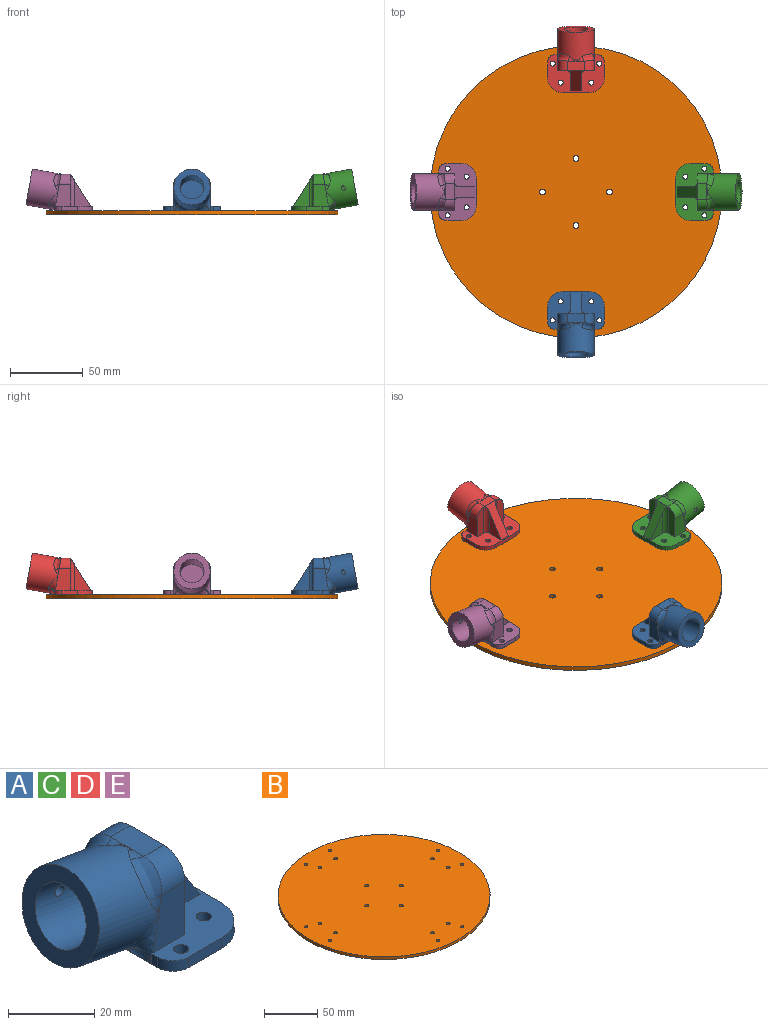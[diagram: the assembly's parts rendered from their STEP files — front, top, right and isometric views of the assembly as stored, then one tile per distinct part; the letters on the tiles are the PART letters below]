
ASSEMBLY  parts=5 mates=1
PART A: 46 faces, bbox 46.3x39.8x31.6 mm
  f0: plane 25x22mm, normal (1,0,0), area 244.4mm2, adj f2,f3,f6,f12,f13,f17,f41,f42
  f1: plane 19x3mm, normal (1,0,0), area 57mm2, adj f7,f17,f44,f45
  f2: plane 15x10.37mm, normal (0,-1,0), area 135.6mm2, adj f0,f13,f17,f27,f34
  f3: plane 15.21x10.58mm, normal (0,1,0), area 135.6mm2, adj f0,f12,f17,f31,f35
  f4: plane 0.66x0.63mm, normal (-0.98,0,0.17), area 0.2mm2, adj f7,f18,f28
  f5: plane 0.66x0.63mm, normal (-0.98,0,0.17), area 0.2mm2, adj f7,f14,f30
  f6: plane 11x6.49mm, normal (0,0,1), area 71.4mm2, adj f0,f12,f13,f32,f37
  f7: plane 39.81x26.71mm, normal (0,0,-1), area 917.8mm2, adj f1,f4,f5,f15,f16,f19,f20,f21
  f8: cylinder r=8.25mm len=22.56mm, axis (0.98,0,-0.17), area 1029.6mm2, adj f10,f11,f38
  f9: cylinder r=12.5mm len=28.09mm, axis (0.98,0,-0.17), area 1320.7mm2, adj f10,f27,f28,f29,f30,f31,f32,f33
  f10: plane 25x24.62mm, normal (-0.98,0,0.17), area 277mm2, adj f8,f9
  f11: plane 16.5x16.25mm, normal (-0.98,0,0.17), area 213.8mm2, adj f8
  f12: cylinder r=7mm len=7.72mm, axis (-1,0,0), area 78.1mm2, adj f0,f3,f6,f36
  f13: cylinder r=7mm len=7.72mm, axis (1,0,0), area 78.1mm2, adj f0,f2,f6,f33
  f14: plane 3.07x0.6mm, normal (0,-1,0), area 0.8mm2, adj f5,f15,f17,f31
  f15: plane 3x2mm, normal (-1,0,0), area 6mm2, adj f7,f14,f17,f26
  f16: plane 10.89x3mm, normal (0,1,0), area 32.7mm2, adj f7,f17,f26,f45
  f17: plane 39x25.89mm, normal (0,0,1), area 543.4mm2, adj f0,f1,f2,f3,f14,f15,f16,f18
  f18: plane 3.07x0.6mm, normal (0,1,0), area 0.8mm2, adj f4,f17,f20,f27
  f19: plane 10.89x3mm, normal (0,-1,0), area 32.7mm2, adj f7,f17,f25,f44
  f20: plane 3x2mm, normal (-1,0,0), area 6mm2, adj f7,f17,f18,f25
  f21: cylinder r=1.75mm len=3.5mm, axis (0,0,1), area 33mm2, adj f7,f17
  f22: cylinder r=1.75mm len=3.5mm, axis (0,0,1), area 33mm2, adj f7,f17
  f23: cylinder r=1.75mm len=3.5mm, axis (0,0,1), area 33mm2, adj f7,f17
  f24: cylinder r=1.75mm len=3.5mm, axis (0,0,1), area 33mm2, adj f7,f17
  f25: cylinder r=5mm len=5mm, axis (0,0,1), area 23.6mm2, adj f7,f17,f19,f20
  f26: cylinder r=5mm len=5mm, axis (0,0,1), area 23.6mm2, adj f7,f15,f16,f17
  f27: bspline ~12.43x6.48mm, area 38.1mm2, adj f2,f9,f18,f28
  f28: torus R=17.5mm, axis (-0.98,0,0.17), area 5.9mm2, adj f4,f9,f27,f29
  f29: bspline ~24.48x5.27mm, area 84.2mm2, adj f7,f9,f28,f30
  f30: torus R=17.5mm, axis (-0.98,0,0.17), area 5.9mm2, adj f5,f9,f29,f31
  f31: bspline ~12.43x6.48mm, area 38.1mm2, adj f3,f9,f14,f30
  f32: bspline ~6.88x3.6mm, area 8mm2, adj f6,f9,f33
  f33: bspline ~8.72x8.55mm, area 48.9mm2, adj f9,f13,f32,f34
  f34: bspline ~5.69x3.22mm, area 7.7mm2, adj f2,f9,f33
  f35: bspline ~5.31x3.02mm, area 7.7mm2, adj f3,f9,f36
  f36: bspline ~9.04x8.48mm, area 48.9mm2, adj f9,f12,f35,f37
  f37: bspline ~5.5x2.91mm, area 8mm2, adj f6,f9,f36
  f38: cylinder r=1.5mm len=4.27mm, axis (0,-1,0), area 40.2mm2, adj f8,f9
  f39: plane 17.2x11.02mm, normal (0,1,0), area 94.8mm2, adj f17,f41,f42
  f40: plane 17.2x11.02mm, normal (0,-1,0), area 94.8mm2, adj f17,f41,f43
  f41: plane 21.89x14.02mm, normal (0.84,0,0.54), area 189.1mm2, adj f0,f17,f39,f40,f42,f43
  f42: cylinder r=3mm len=21.89mm, axis (0,0,1), area 95.1mm2, adj f0,f17,f39,f41
  f43: cylinder r=3mm len=21.89mm, axis (0,0,-1), area 95.1mm2, adj f0,f17,f40,f41
  f44: cylinder r=10mm len=10mm, axis (0,0,-1), area 47.1mm2, adj f1,f7,f17,f19
  f45: cylinder r=10mm len=10mm, axis (0,0,1), area 47.1mm2, adj f1,f7,f16,f17
PART B: 23 faces, bbox 200x200x3 mm
  f0: cylinder r=100mm len=200mm, axis (0,0,-1), area 1885mm2, adj f1,f2
  f1: plane 200x200mm, normal (0,0,1), area 31211.7mm2, adj f0,f3,f4,f5,f6,f7,f8,f9
  f2: plane 200x200mm, normal (0,0,-1), area 31211.7mm2, adj f0,f3,f4,f5,f6,f7,f8,f9
  f3: cylinder r=1.75mm len=3.5mm, axis (0,0,1), area 33mm2, adj f1,f2
  f4: cylinder r=1.75mm len=3.5mm, axis (0,0,1), area 33mm2, adj f1,f2
  f5: cylinder r=1.75mm len=3.5mm, axis (0,0,1), area 33mm2, adj f1,f2
  f6: cylinder r=1.75mm len=3.5mm, axis (0,0,1), area 33mm2, adj f1,f2
  f7: cylinder r=1.75mm len=3.5mm, axis (0,0,1), area 33mm2, adj f1,f2
  f8: cylinder r=1.75mm len=3.5mm, axis (0,0,1), area 33mm2, adj f1,f2
  f9: cylinder r=1.75mm len=3.5mm, axis (0,0,1), area 33mm2, adj f1,f2
  f10: cylinder r=1.75mm len=3.5mm, axis (0,0,1), area 33mm2, adj f1,f2
  f11: cylinder r=1.75mm len=3.5mm, axis (0,0,1), area 33mm2, adj f1,f2
  f12: cylinder r=1.75mm len=3.5mm, axis (0,0,1), area 33mm2, adj f1,f2
  f13: cylinder r=1.75mm len=3.5mm, axis (0,0,1), area 33mm2, adj f1,f2
  f14: cylinder r=1.75mm len=3.5mm, axis (0,0,1), area 33mm2, adj f1,f2
  f15: cylinder r=1.75mm len=3.5mm, axis (0,0,1), area 33mm2, adj f1,f2
  f16: cylinder r=1.75mm len=3.5mm, axis (0,0,1), area 33mm2, adj f1,f2
  f17: cylinder r=1.75mm len=3.5mm, axis (0,0,1), area 33mm2, adj f1,f2
  f18: cylinder r=1.75mm len=3.5mm, axis (0,0,1), area 33mm2, adj f1,f2
  f19: cylinder r=2mm len=4mm, axis (0,0,1), area 37.7mm2, adj f1,f2
  f20: cylinder r=2mm len=4mm, axis (0,0,1), area 37.7mm2, adj f1,f2
  f21: cylinder r=2mm len=4mm, axis (0,0,1), area 37.7mm2, adj f1,f2
  f22: cylinder r=2mm len=4mm, axis (0,0,1), area 37.7mm2, adj f1,f2
PART C: same geometry as A
PART D: same geometry as A
PART E: same geometry as A
PLACE A rot(axis=(0,0,1),90deg) t=(-43.78,-77.64,38.59)mm
PLACE B t=(-43.78,5.61,23.09)mm
PLACE C rot(axis=(0,0,1),180deg) t=(39.47,5.61,38.59)mm
PLACE D rot(axis=(0,0,-1),90deg) t=(-43.78,88.86,38.59)mm
PLACE E t=(-127.03,5.61,38.59)mm
MATE fastened B.f8 <-> E.f22  axis (0,0,1) through (-118.78,-4.89,26.09)mm
